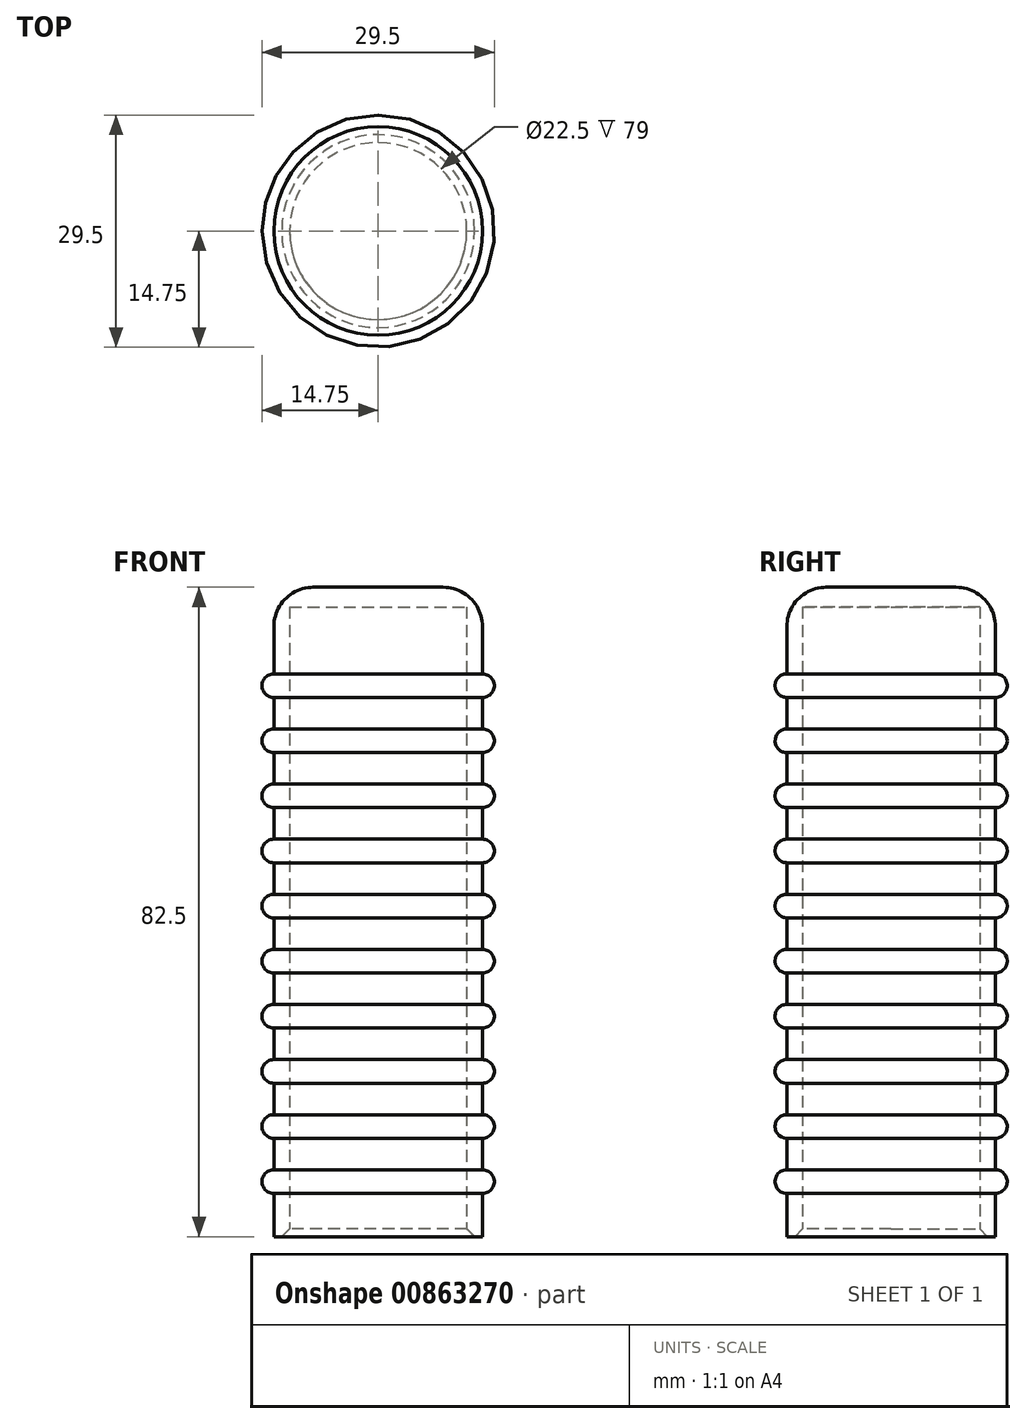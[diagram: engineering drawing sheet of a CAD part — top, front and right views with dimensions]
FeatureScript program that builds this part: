
annotation { "Feature Type Name" : "Feature", "Feature Type Description" : "" }
export const myFeature = defineFeature(function(context is Context, id is Id, definition is map)
    precondition{}
    {
        {
            var Q0;
            Q0=qCreatedBy(makeId("Front.planeOp"),FACE);
            var sketch = newSketch(context, id + "F0", { "sketchPlane" : qUnion([Q0])});
            skLineSegment(sketch, "E0", {"start": v(0, 0) * mm, "end": v(0, 82.5) * mm});
            skLineSegment(sketch, "E1", {"start": v(0, 82.5) * mm, "end": v(8.25, 82.5) * mm});
            skLineSegment(sketch, "E2", {"start": v(13.25, 77.5) * mm, "end": v(13.25, 0) * mm});
            skLineSegment(sketch, "E3", {"start": v(13.25, 0) * mm, "end": v(11.25, 0) * mm});
            skLineSegment(sketch, "E4", {"start": v(11.25, 0) * mm, "end": v(11.25, 80) * mm});
            skLineSegment(sketch, "E5", {"start": v(11.25, 80) * mm, "end": v(0, 80) * mm});
            skPoint(sketch, "E6.visualSharp", {"position": v(13.25, 82.5) * mm});
            skArc(sketch, "E6.filletArc", {"start": v(13.25, 77.5) * mm, "mid": v(11.79, 81.04) * mm, "end": v(8.25, 82.5) * mm});
            skArc(sketch, "E7", {"start": v(13.25, 5.5) * mm, "mid": v(14.75, 7) * mm, "end": v(13.25, 8.5) * mm});
            skArc(sketch, "E8.0.1.0", {"start": v(13.25, 12.5) * mm, "mid": v(14.75, 14) * mm, "end": v(13.25, 15.5) * mm});
            skArc(sketch, "E8.0.2.0", {"start": v(13.25, 19.5) * mm, "mid": v(14.75, 21) * mm, "end": v(13.25, 22.5) * mm});
            skArc(sketch, "E8.0.3.0", {"start": v(13.25, 26.5) * mm, "mid": v(14.75, 28) * mm, "end": v(13.25, 29.5) * mm});
            skArc(sketch, "E8.0.4.0", {"start": v(13.25, 33.5) * mm, "mid": v(14.75, 35) * mm, "end": v(13.25, 36.5) * mm});
            skArc(sketch, "E8.0.5.0", {"start": v(13.25, 40.5) * mm, "mid": v(14.75, 42) * mm, "end": v(13.25, 43.5) * mm});
            skArc(sketch, "E8.0.6.0", {"start": v(13.25, 47.5) * mm, "mid": v(14.75, 49) * mm, "end": v(13.25, 50.5) * mm});
            skArc(sketch, "E8.0.7.0", {"start": v(13.25, 54.5) * mm, "mid": v(14.75, 56) * mm, "end": v(13.25, 57.5) * mm});
            skArc(sketch, "E8.0.8.0", {"start": v(13.25, 61.5) * mm, "mid": v(14.75, 63) * mm, "end": v(13.25, 64.5) * mm});
            skArc(sketch, "E8.0.9.0", {"start": v(13.25, 68.5) * mm, "mid": v(14.75, 70) * mm, "end": v(13.25, 71.5) * mm});
            skLineSegment(sketch, "E8.direction1", {"start": v(13.25, 7) * mm, "end": v(38.75, 7) * mm, "construction": true});
            skLineSegment(sketch, "E8.direction2", {"start": v(13.25, 7) * mm, "end": v(13.25, 14) * mm, "construction": true});
            skSolve(sketch);
        }
        {
            var Q0;
            Q0 = qSketchRegion(id + "F0", true);
            var Q1;
            Q1=sQuery(id+"F0.wireOp",EDGE,"E0");
            revolve(context, id + "F1", {"surfaceOperationType" : NewSurfaceOperationType.NEW, "entities" : qUnion([Q0]), "axis" : qUnion([Q1]), "revolveType" : RevolveType.FULL});
        }
        {
            var Q0;
            Q0=makeQuery(id+"F1.opRevolve","SWEPT_EDGE",EDGE,{"disambiguationData":[OSD([sQuery(id+"F0.wireOp",EDGE,"E3"),sQuery(id+"F0.wireOp",EDGE,"E4")])]});
            chamfer(context, id + "F2", {"entities" : qUnion([Q0]), "width" : 1 * mm, "tangentPropagation" : true});
        }
    });
